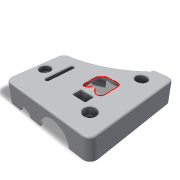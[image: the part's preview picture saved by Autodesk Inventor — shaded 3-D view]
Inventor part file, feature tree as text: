
AUTODESK INVENTOR PART (.ipt)
format: ipt  version: 2016 (Build 200138000, 138)  size: 935,424 bytes
history: native  units: in
note: dims shown in document units (in); Inventor stores cm internally (conversion verified against a paired STEP export)
features: sketch x21, extrude x17, projected_geometry x11, fillet x6, plane x3, other x2, loft x1, imported_body x1
ambient origin geometry x8: Origin, YZ Plane, XZ Plane, XY Plane, X Axis, Y Axis, Z Axis, Center Point
bodies: Solid1 (feature_tree)
feature tree (62):
  other  "032-Fe_Top_Cover-0601-3_stp.ipt1"
  sketch  "Sketch2"  dims[d7=0.1181in d8=0.1181in]
  other  "Work Axis1"
  plane  "Work Plane1"
  extrude  "Extrusion2"  Depth=0.1181in
  plane  "Work Plane3"
  loft  "Loft1"
  extrude  "Extrusion4"  Depth=0.1575in
  extrude  "Extrusion5"  TaperAngle=0.0deg  [1 undecoded]
  extrude  "Extrusion6"  TaperAngle=0.0deg  [1 undecoded]
  extrude  "Extrusion7"  Depth=0.1181in
  extrude  "Extrusion8"  Depth=0.0591in
  fillet  "Fillet5"  Radius=0.0197in
  fillet  "Fillet6"  Radius=0.0787in
  extrude  "Extrusion9"  Depth=0.3937in
  extrude  "Extrusion10"  Depth=0.7087in
  extrude  "Extrusion12"  Depth=0.0118in
  extrude  "Extrusion13"  Depth=0.0315in
  extrude  "Extrusion14"  Depth=0.2559in
  extrude  "Extrusion15"  Depth=0.3937in TaperAngle=0.0deg
  sketch  "Sketch20"  dims[d78=0.1575in d79=0.1575in]
  extrude  "Extrusion17"  Depth=0.5512in
  extrude  "Extrusion19"  Depth=0.2362in
  extrude  "Extrusion20"  Depth=0.4252in
  fillet  "Fillet7"  Radius=0.4724in
  fillet  "Fillet8"  Radius=0.4724in
  extrude  "Extrusion21"  Depth=0.1575in
  extrude  "Extrusion22"  Depth=0.4724in
  fillet  "Fillet9"  Radius=0.0394in
  fillet  "Fillet10"  Radius=0.0039in
  imported_body  "Base1"
  sketch  "Sketch3"  dims[d9=0.3937in d10=0.0137in d14=0.1575in d15=0.2047in]
  plane  "Work Plane2"
  sketch  "Sketch5"  dims[d16=0.0906in d17=0.1575in]
  sketch  "Sketch6"  dims[d18=0.4331in d19=0.0in d20=90.0deg]
  sketch  "Sketch7"  dims[d21=0.0in d22=90.0deg d23=0.0in d24=90.0deg]
  sketch  "Sketch8"  dims[d25=0.3937in d26=0.0in d29=0.1181in]
  sketch  "Sketch9"  dims[d30=0.0591in d31=0.0591in d32=0.0197in d33=0.0in d34=0.0787in]
  sketch  "Sketch10"  dims[d35=0.1575in d36=0.3937in d37=0.0137in]
  sketch  "Sketch11"  dims[d39=0.0in d40=0.0in d42=0.7087in]
  sketch  "Sketch12"  dims[d43=0.3543in d44=-0.0137in d45=0.0118in]
  sketch  "Sketch13"  dims[d46=0.0118in d47=0.0315in d48=-0.0103in]
  projected_geometry  "Projected Loop4"
  sketch  "Sketch14"  dims[d49=0.0236in d50=0.0in d51=0.2559in]
  sketch  "Sketch16"  dims[d55=0.4724in d56=0.3937in d57=0.0in]
  projected_geometry  "Projected Loop6"
  sketch  "Sketch17"  dims[d58=0.4724in d59=0.0137in d60=0.5512in]
  projected_geometry  "Projected Loop7"
  sketch  "Sketch18"  dims[d61=0.5394in d62=0.2362in]
  projected_geometry  "Projected Loop8"
  sketch  "Sketch19"  dims[d63=0.4724in d64=0.0in d65=0.4252in d66=0.4724in d67=0.0137in d74=0.4724in d75=0.0137in]
  projected_geometry  "Projected Loop9"
  projected_geometry  "Projected Loop10"
  projected_geometry  "Projected Loop11"
  sketch  "Sketch21"  dims[d80=0.4724in d81=-0.0137in d82=0.4724in d83=0.0137in d84=0.0394in d85=0.0039in]
  projected_geometry  "Projected Loop12"
  sketch  "Sketch22"  dims[d86=0.4724in d87=0.0103in]
  projected_geometry  "Projected Loop13"
  sketch  "Sketch23"  dims[d88=0.4724in d89=0.0103in]
  projected_geometry  "Projected Loop14"
  sketch  "Sketch24"  dims[d90=0.0118in d91=0.0394in]
  projected_geometry  "Projected Loop15"
note: 2 required parameter values undecoded (feature->parameter linkage not recoverable at this tier; creation-order binding heuristic only, values carry confidence <= 0.55)
